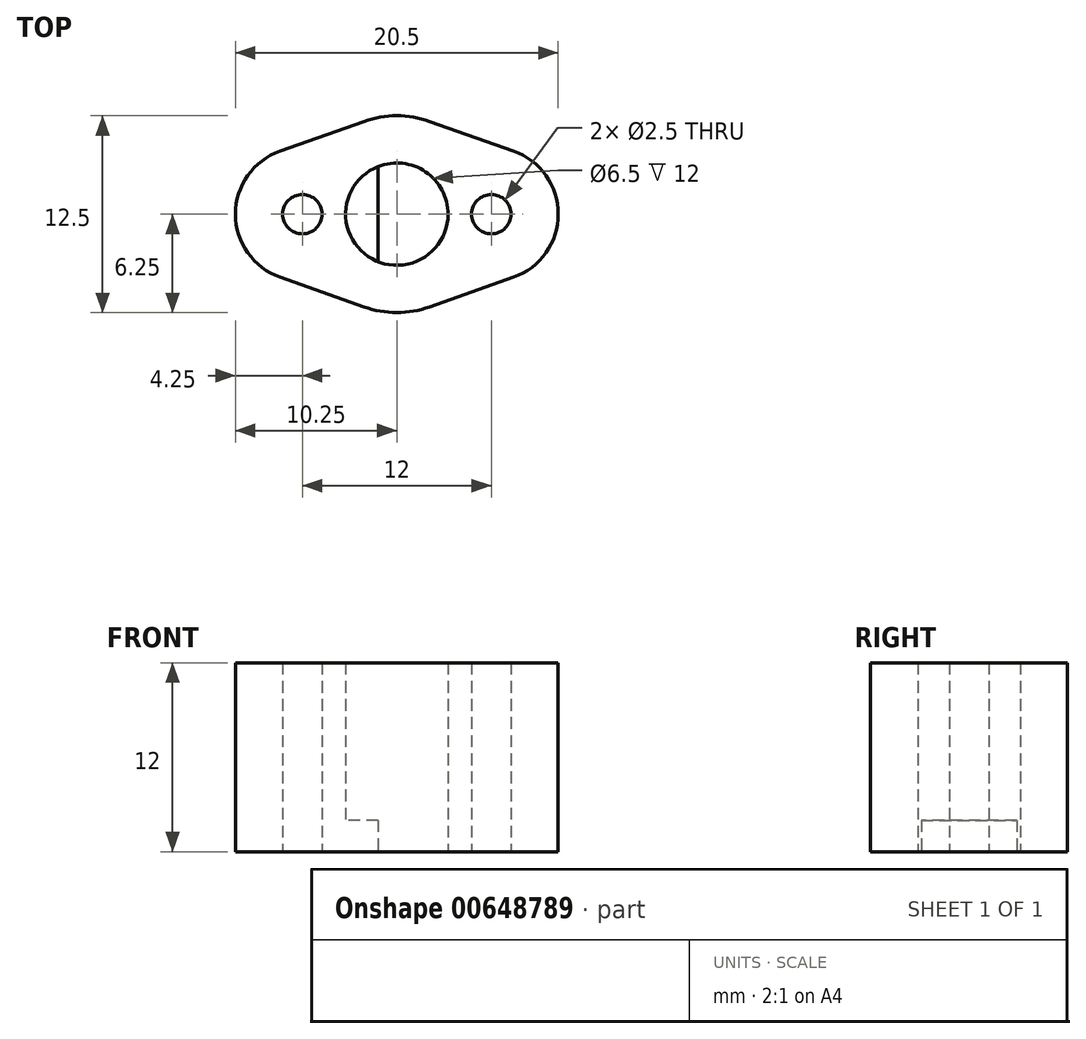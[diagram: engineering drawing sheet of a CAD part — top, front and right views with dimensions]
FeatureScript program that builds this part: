
annotation { "Feature Type Name" : "Feature", "Feature Type Description" : "" }
export const myFeature = defineFeature(function(context is Context, id is Id, definition is map)
    precondition{}
    {
        {
            var Q0;
            Q0=qCreatedBy(makeId("Top.planeOp"),FACE);
            var sketch = newSketch(context, id + "F0", { "sketchPlane" : qUnion([Q0])});
            skCircle(sketch, "E0", {"center": v(0, 0) * mm, "radius": 3.25 * mm});
            skCircle(sketch, "E1", {"center": v(6, 0) * mm, "radius": 1.25 * mm});
            skArc(sketch, "E2", {"start": v(7.42, 4) * mm, "mid": v(10.25, 0) * mm, "end": v(7.42, -4) * mm});
            skLineSegment(sketch, "E3", {"start": v(2.08, 5.9) * mm, "end": v(7.42, 4) * mm});
            skLineSegment(sketch, "E4", {"start": v(2.08, -5.9) * mm, "end": v(7.42, -4) * mm});
            skCircle(sketch, "E5.MirrorC", {"center": v(-6, 0) * mm, "radius": 1.25 * mm});
            skArc(sketch, "E6.MirrorCS", {"start": v(-7.42, 4) * mm, "mid": v(-10.25, 0) * mm, "end": v(-7.42, -4) * mm});
            skLineSegment(sketch, "E7.MirrorCS", {"start": v(-2.08, 5.9) * mm, "end": v(-7.42, 4) * mm});
            skLineSegment(sketch, "E8.MirrorCS", {"start": v(-2.08, -5.9) * mm, "end": v(-7.42, -4) * mm});
            skArc(sketch, "E9", {"start": v(-2.08, 5.9) * mm, "mid": v(0, 6.25) * mm, "end": v(2.08, 5.9) * mm});
            skArc(sketch, "E10", {"start": v(-2.08, -5.9) * mm, "mid": v(0, -6.25) * mm, "end": v(2.08, -5.9) * mm});
            skSolve(sketch);
        }
        {
            var Q0;
            Q0=makeQuery(id+"F0.imprint","IMPRINT",FACE,{"disambiguationData":[TD([[makeQuery(id+"F0.imprint","IMPRINT",EDGE,{"derivedFrom":sQuery(id+"F0.wireOp",EDGE,"E0")}),-1.0]])]});
            extrude(context, id + "F1", {"entities" : qUnion([Q0]), "depth" : 12 * mm, "offsetDistance" : 25 * mm});
        }
        {
            var Q0;
            Q0=makeQuery(id+"F1.opExtrude","CAP_FACE",FACE,{"disambiguationData":[OSD([sQuery(id+"F0.wireOp",EDGE,"E0"),sQuery(id+"F0.wireOp",EDGE,"E1"),sQuery(id+"F0.wireOp",EDGE,"E2"),sQuery(id+"F0.wireOp",EDGE,"E3"),sQuery(id+"F0.wireOp",EDGE,"E4"),sQuery(id+"F0.wireOp",EDGE,"E5.MirrorC"),sQuery(id+"F0.wireOp",EDGE,"E6.MirrorCS"),sQuery(id+"F0.wireOp",EDGE,"E7.MirrorCS"),sQuery(id+"F0.wireOp",EDGE,"E8.MirrorCS"),sQuery(id+"F0.wireOp",EDGE,"E9"),sQuery(id+"F0.wireOp",EDGE,"E10")])],"isStart":true});
            var sketch = newSketch(context, id + "F2", { "sketchPlane" : qUnion([Q0])});
            skLineSegment(sketch, "E11", {"start": v(-1.18, 3.03) * mm, "end": v(-1.18, -3.03) * mm});
            skSolve(sketch);
        }
        {
            var Q0;
            {var subQ0=sQuery(id+"F2.wireOp",EDGE,"E11");Q0=makeQuery(id+"F2.imprint","IMPRINT",FACE,{"disambiguationData":[TD([[makeQuery(id+"F2.imprint","IMPRINT",EDGE,{"derivedFrom":subQ0}),-1.0]])]});}
            extrude(context, id + "F3", {"entities" : qUnion([Q0]), "operationType" : NewBodyOperationType.ADD, "oppositeDirection" : true, "depth" : 2 * mm, "offsetDistance" : 25 * mm});
        }
    });
